# Revit family: R SONNIGER - Nagrzewnica wodna HEATER CONDENS - CR ONE, CR1, CR2, CR3, CR3 MAX, CR4 MAX
name_source: partatom
category: Wyposażenie mechaniczne
revit_build: Autodesk Revit 2018 (Build: 20170927_1515(x64)
units: mm (PartAtom-declared; Revit-internal decimal feet)

## family parameters
Klasyfikacja = Brak
Obiekt nadrzędny = Powierzchnia
Punkt obliczania pomieszczeń = Nie
Tnij formami wycięć po wczytaniu = Nie
Typ części = Normalny
Współdzielony = Nie
Wymiar okrągłego złącza = Użyj średnicy

## types (14) — shared parameters
Domyślna rzędna = 1219.200 mm
O = 130.000 mm
Opis = Водяной тепловентилятор
Producent = SONNIGER Polska Sp. z o.o. Sp. k.
автор = www.archispace.com
класс IP = IP54
максимальная темп. Теплоносителя = 120 °C
максимальное рабочее давление = 1600000.0 Pa
материал = 230,230,230
напряжение питания = 230 V
zero-valued in all types: Уровень шума

## per-type parameters (varying)
| type | H | Model | O1 | S g | W g | ΔT | Количество рядов нагревателя | Максимальная длина воздушного потока | Масса оборудования | Мощность обогрева max. | Мощность обогрева min. | Мощность электродвигателя | максимальный расход воздуха | масса оборудования с водой | уровень шума | частота вращения двигателя |
| CR ONE - настенный монтаж | 18536.143 mm | Heater CONDENS CR ONE | Tak | 13120.000 mm | 13850.000 mm | 25 °C | 2 | 14000.000 mm | 9.60 kg | 25 kW | 5 kW | 124 W | 1600.0 m³/h | 10.70 kg | I скорость 35 dB / II скорость 46 dB / III скорость 52 dB | 1400 |
| CR1 - настенный монтаж | 26136.143 mm | Heater CONDENS CR1 | Tak | 16000.000 mm | 16000.000 mm | 13 °C | 1 | 24000.000 mm | 10.80 kg | 35 kW | 10 kW | 250 W | 3900.0 m³/h | 11.90 kg | I скорость 44 dB / II скорость 52 dB / III скорость 62 dB | 1350 |
| CR2 - настенный монтаж | 24536.143 mm | Heater CONDENS CR2 | Tak | 15900.000 mm | 15100.000 mm | 22 °C | 2 | 21000.000 mm | 12.70 kg | 50 kW | 15 kW | 250 W | 3350.0 m³/h | 14.80 kg | I скорость 41 dB / II скорость 50 dB / III скорость 60 dB | 1350 |
| CR3 - настенный монтаж | 22936.143 mm | Heater CONDENS CR3 | Tak | 15400.000 mm | 14600.000 mm | 34 °C | 3 | 19000.000 mm | 14.50 kg | 70 kW | 20 kW | 250 W | 2950.0 m³/h | 16.90 kg | I скорость 39 dB / II скорость 48 dB / III скорость 58 dB | 1350 |
| CR ONE - потолочный монтаж | 9536.143 mm | Heater CONDENS CR ONE | Tak | 9100.000 mm | 9900.000 mm | 25 °C | 2 | 14000.000 mm | 9.60 kg | 25 kW | 5 kW | 124 W | 1600.0 m³/h | 10.70 kg | I скорость 35 dB / II скорость 46 dB / III скорость 52 dB | 1400 |
| CR1 - потолочный монтаж | 12536.143 mm | Heater CONDENS CR1 | Tak | 11420.000 mm | 10510.000 mm | 13 °C | 1 | 24000.000 mm | 10.80 kg | 35 kW | 10 kW | 250 W | 3900.0 m³/h | 11.90 kg | I скорость 44 dB / II скорость 52 dB / III скорость 62 dB | 1350 |
| CR2 - потолочный монтаж | 11836.143 mm | Heater CONDENS CR2 | Tak | 10900.000 mm | 10360.000 mm | 22 °C | 2 | 21000.000 mm | 12.70 kg | 50 kW | 15 kW | 250 W | 3350.0 m³/h | 14.80 kg | I скорость 41 dB / II скорость 50 dB / III скорость 60 dB | 1350 |
| CR3 - потолочный монтаж | 11036.143 mm | Heater CONDENS CR3 | Tak | 10760.000 mm | 9760.000 mm | 34 °C | 3 | 19000.000 mm | 14.50 kg | 70 kW | 20 kW | 250 W | 2950.0 m³/h | 16.90 kg | I скорость 39 dB / II скорость 48 dB / III скорость 58 dB | 1350 |
| CR2 MAX - потолочный монтаж | 14860.341 mm | Heater CONDENS CR2 MAX | Nie | 12470.000 mm | 11470.000 mm | 22 °C | 2 | 26000.000 mm | 23.60 kg | 70 kW | 25 kW | 520 W | 5700.0 m³/h | 25.20 kg | I скорость 41 dB / II скорость 50 dB / III скорость 59 dB | 1380 |
| CR2 MAX - настенный монтаж | 13536.341 mm | Heater CONDENS CR2 MAX | Nie | 19500.000 mm | 19500.000 mm | 22 °C | 2 | 26000.000 mm | 23.60 kg | 70 kW | 25 kW | 520 W | 5700.0 m³/h | 25.20 kg | I скорость 41 dB / II скорость 50 dB / III скорость 59 dB | 1380 |
| CR3 MAX - потолочный монтаж | 14060.341 mm | Heater CONDENS CR3 MAX | Nie | 12000.000 mm | 11250.000 mm | 35 °C | 3 | 25000.000 mm | 25.20 kg | 95 kW | 35 kW | 520 W | 5600.0 m³/h | 27.40 kg | I скорость 40 dB / II скорость 48 dB / III скорость 58 dB | 1380 |
| CR3 MAX - настенный монтаж | 31160.341 mm | Heater CONDENS CR3 MAX | Nie | 17900.000 mm | 17100.000 mm | 35 °C | 3 | 25000.000 mm | 25.50 kg | 95 kW | 35 kW | 520 W | 5600.0 m³/h | 27.40 kg | I скорость 40 dB / II скорость 48 dB / III скорость 58 dB | 1380 |
| CR4 MAX - потолочный монтаж | 13360.341 mm | Heater CONDENS CR4 MAX | Nie | 11820.000 mm | 10830.000 mm | 44 °C | 3 | 23000.000 mm | 25.50 kg | 120 kW | 40 kW | 520 W | 5100.0 m³/h | 28.00 kg | I скорость 40 dB / II скорость 48 dB / III скорость 58 dB | 1380 |
| CR4 MAX - настенный монтаж | 32860.341 mm | Heater CONDENS CR4 MAX | Nie | 18400.000 mm | 17550.000 mm | 44 °C | 3 | 23000.000 mm | 25.50 kg | 120 kW | 40 kW | 520 W | 5100.0 m³/h | 28.00 kg | I скорость 40 dB / II скорость 48 dB / III скорость 58 dB | 1380 |
